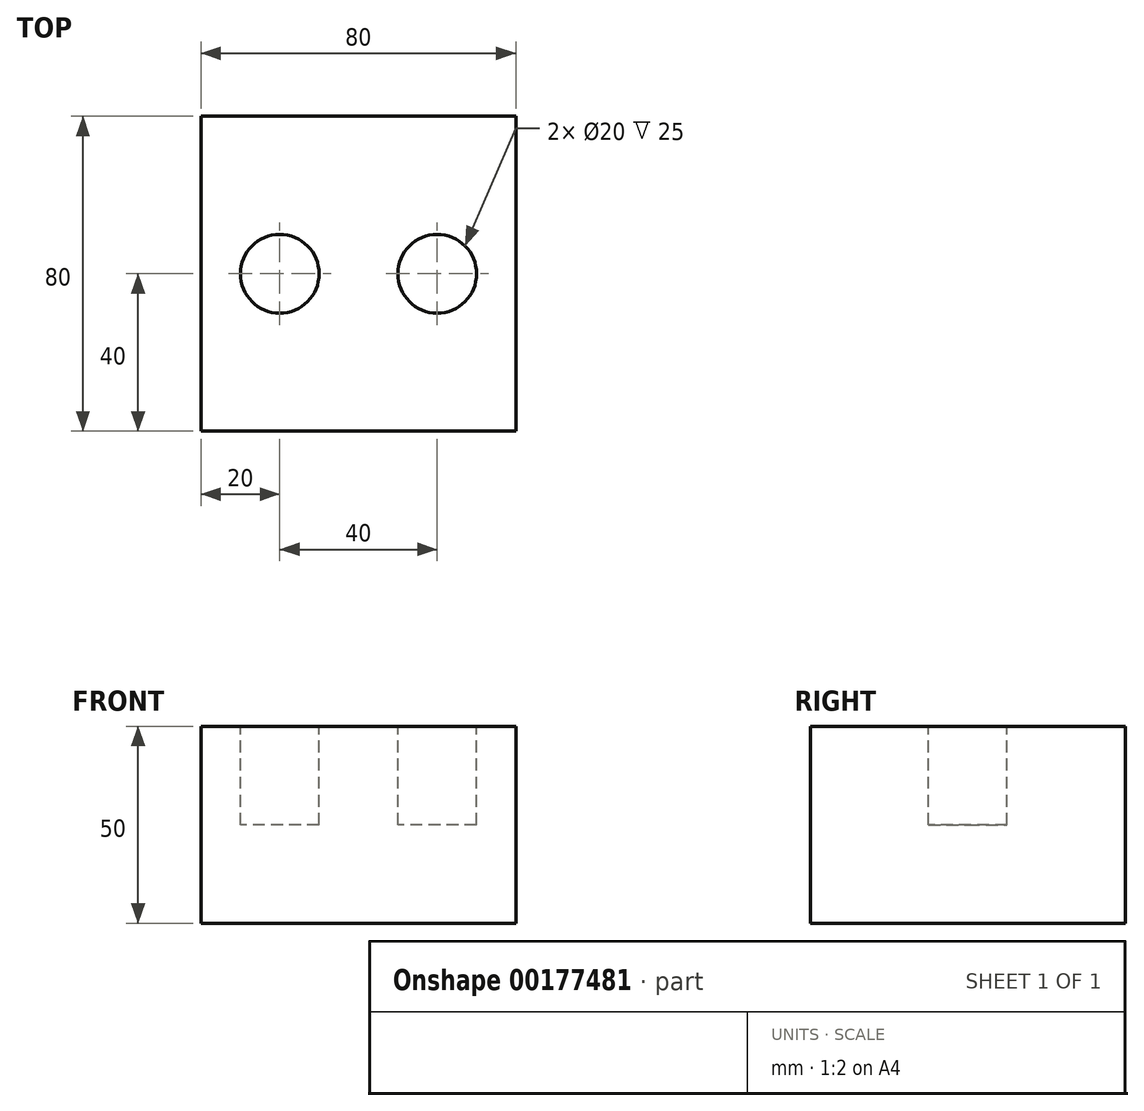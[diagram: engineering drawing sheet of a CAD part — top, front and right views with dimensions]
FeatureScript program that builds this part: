
annotation { "Feature Type Name" : "Feature", "Feature Type Description" : "" }
export const myFeature = defineFeature(function(context is Context, id is Id, definition is map)
    precondition{}
    {
        {
            var Q0;
            Q0=qCreatedBy(makeId("Top.planeOp"),FACE);
            var sketch = newSketch(context, id + "F0", { "sketchPlane" : qUnion([Q0])});
            skLineSegment(sketch, "E0.bottom", {"start": v(40, 40) * mm, "end": v(-40, 40) * mm});
            skLineSegment(sketch, "E0.top", {"start": v(40, -40) * mm, "end": v(-40, -40) * mm});
            skLineSegment(sketch, "E0.left", {"start": v(40, 40) * mm, "end": v(40, -40) * mm});
            skLineSegment(sketch, "E0.right", {"start": v(-40, 40) * mm, "end": v(-40, -40) * mm});
            skPoint(sketch, "E0.middle", {"position": v(0, 0) * mm});
            skSolve(sketch);
        }
        {
            var Q0;
            Q0=makeQuery(id+"F0.imprint","IMPRINT",FACE,{"disambiguationData":[TD([[makeQuery(id+"F0.imprint","IMPRINT",EDGE,{"derivedFrom":sQuery(id+"F0.wireOp",EDGE,"E0.bottom")}),1.0]])]});
            extrude(context, id + "F1", {"entities" : qUnion([Q0]), "depth" : 50 * mm});
        }
        {
            var Q0;
            Q0=makeQuery(id+"F1.opExtrude","CAP_FACE",FACE,{"disambiguationData":[OSD([sQuery(id+"F0.wireOp",EDGE,"E0.bottom"),sQuery(id+"F0.wireOp",EDGE,"E0.top"),sQuery(id+"F0.wireOp",EDGE,"E0.left"),sQuery(id+"F0.wireOp",EDGE,"E0.right")])],"isStart":false});
            var sketch = newSketch(context, id + "F2", { "sketchPlane" : qUnion([Q0])});
            skCircle(sketch, "E1", {"center": v(-20, 0) * mm, "radius": 10 * mm});
            skCircle(sketch, "E2", {"center": v(20, 0) * mm, "radius": 10 * mm});
            skSolve(sketch);
        }
        {
            var Q0;
            Q0=makeQuery(id+"F2.imprint","IMPRINT",FACE,{"disambiguationData":[TD([[makeQuery(id+"F2.imprint","IMPRINT",EDGE,{"derivedFrom":sQuery(id+"F2.wireOp",EDGE,"E1")}),1.0]])]});
            var Q1;
            Q1=makeQuery(id+"F2.imprint","IMPRINT",FACE,{"disambiguationData":[TD([[makeQuery(id+"F2.imprint","IMPRINT",EDGE,{"derivedFrom":sQuery(id+"F2.wireOp",EDGE,"E2")}),1.0]])]});
            extrude(context, id + "F3", {"entities" : qUnion([Q0, Q1]), "operationType" : NewBodyOperationType.REMOVE, "oppositeDirection" : true, "depth" : 25 * mm});
        }
    });
